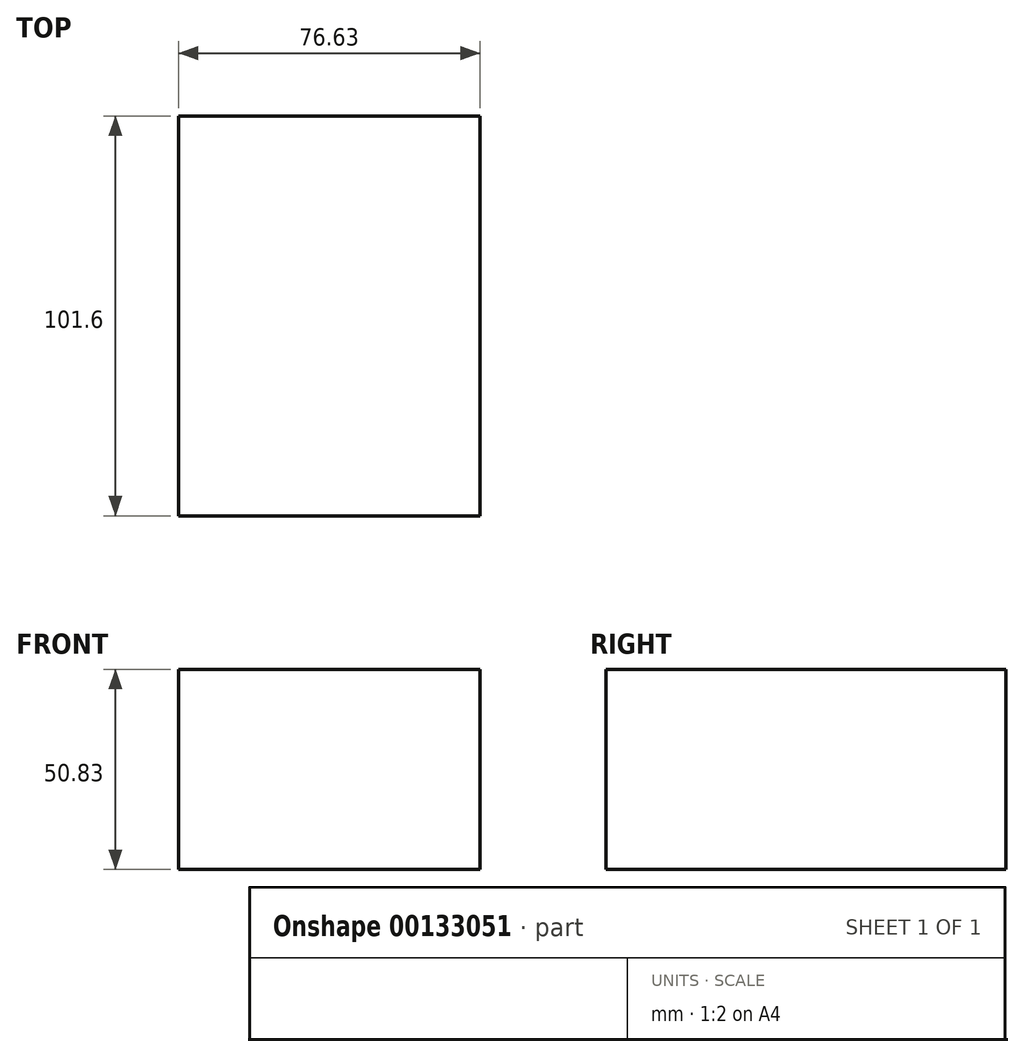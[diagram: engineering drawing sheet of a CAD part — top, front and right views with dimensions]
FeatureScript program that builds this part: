
annotation { "Feature Type Name" : "Feature", "Feature Type Description" : "" }
export const myFeature = defineFeature(function(context is Context, id is Id, definition is map)
    precondition{}
    {
        {
            var Q0;
            Q0=qCreatedBy(makeId("Front.planeOp"),FACE);
            var sketch = newSketch(context, id + "F0", { "sketchPlane" : qUnion([Q0])});
            skLineSegment(sketch, "E0.bottom", {"start": v(-34.94, 26.4) * mm, "end": v(41.7, 26.4) * mm});
            skLineSegment(sketch, "E0.top", {"start": v(-34.94, -24.42) * mm, "end": v(41.7, -24.42) * mm});
            skLineSegment(sketch, "E0.left", {"start": v(-34.94, 26.4) * mm, "end": v(-34.94, -24.42) * mm});
            skLineSegment(sketch, "E0.right", {"start": v(41.7, 26.4) * mm, "end": v(41.7, -24.42) * mm});
            skSolve(sketch);
        }
        {
            var Q0;
            Q0=makeQuery(id+"F0.imprint","IMPRINT",FACE,{"disambiguationData":[TD([[makeQuery(id+"F0.imprint","IMPRINT",EDGE,{"derivedFrom":sQuery(id+"F0.wireOp",EDGE,"E0.bottom")}),-1.0]])]});
            extrude(context, id + "F1", {"entities" : qUnion([Q0]), "depth" : 101.6 * mm});
        }
    });
